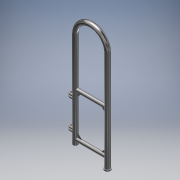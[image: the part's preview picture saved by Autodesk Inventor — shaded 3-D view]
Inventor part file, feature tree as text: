
AUTODESK INVENTOR PART (.ipt)
format: ipt  version: 2018 (Build 220112000, 112)  size: 289,792 bytes
history: native  units: in
note: dims shown in document units (in); Inventor stores cm internally (conversion verified against a paired STEP export)
features: sketch x9, projected_geometry x8, extrude x6, hole x2, sweep x1, plane x1, fillet x1
ambient origin geometry x8: Origin, YZ Plane, XZ Plane, XY Plane, X Axis, Y Axis, Z Axis, Center Point
bodies: Solid1 (feature_tree)
feature tree (28):
  extrude  "Extrusion1"  Depth=2.0in
  sweep  "Sweep1"
  plane  "Work Plane1"
  extrude  "Extrusion2"  [1 undecoded]
  extrude  "Extrusion3"  Depth=20.0in
  fillet  "Fillet1"  Radius=1.5in
  hole  "Hole1"  [1 undecoded]
  extrude  "Extrusion4"  Depth=0.5in
  extrude  "Extrusion5"  Depth=0.5in
  extrude  "Extrusion6"  Depth=0.5in
  hole  "Hole2"  [1 undecoded]
  sketch  "Sketch1"  dims[d0=2.0in d1=2.0in]
  sketch  "Sketch2"  dims[d2=13.5in d3=40.0in d4=0.0in]
  sketch  "Sketch3"  dims[d5=0.0in d6=0.0in d7=-6.75in]
  projected_geometry  "Projected Loop1"
  projected_geometry  "Projected Loop2"
  sketch  "Sketch4"  dims[d8=1.5in d9=20.0in d10=1.5in]
  sketch  "Sketch5"  dims[d11=2.0in d12=6.5in d13=0.0in]
  projected_geometry  "Projected Loop3"
  sketch  "Sketch6"  dims[d15=0.5in d16=0.5in]
  sketch  "Sketch7"  dims[d17=0.5in d18=0.5in]
  sketch  "Sketch8"  dims[d19=0.5in d20=0.5in]
  sketch  "Sketch9"  dims[d22=2.5in d23=0.0in d24=1.0in d26=2.0in d27=1.0in d28=1.75in d29=0.75in d30=0.75in d31=0.375in d32=0.25in d33=0.5635in d34=1.0in d35=0.8108in d39=1.5in d52=0.25in d53=0.0in d54=2.5in d55=0.0in d56=2.5in d57=0.5in d58=0.0in d74=0.417in d75=1.0in d76=0.375in d77=0.25in d78=0.5635in d79=1.385in d80=0.8108in d83=0.5in d84=1.5in d85=0.5in d86=0.5in d87=0.5in d88=4.5in]
  projected_geometry  "Projected Loop5"
  projected_geometry  "Projected Loop9"
  projected_geometry  "Projected Loop10"
  projected_geometry  "Projected Loop11"
  projected_geometry  "Projected Loop12"
note: 3 required parameter values undecoded (feature->parameter linkage not recoverable at this tier; creation-order binding heuristic only, values carry confidence <= 0.55)
